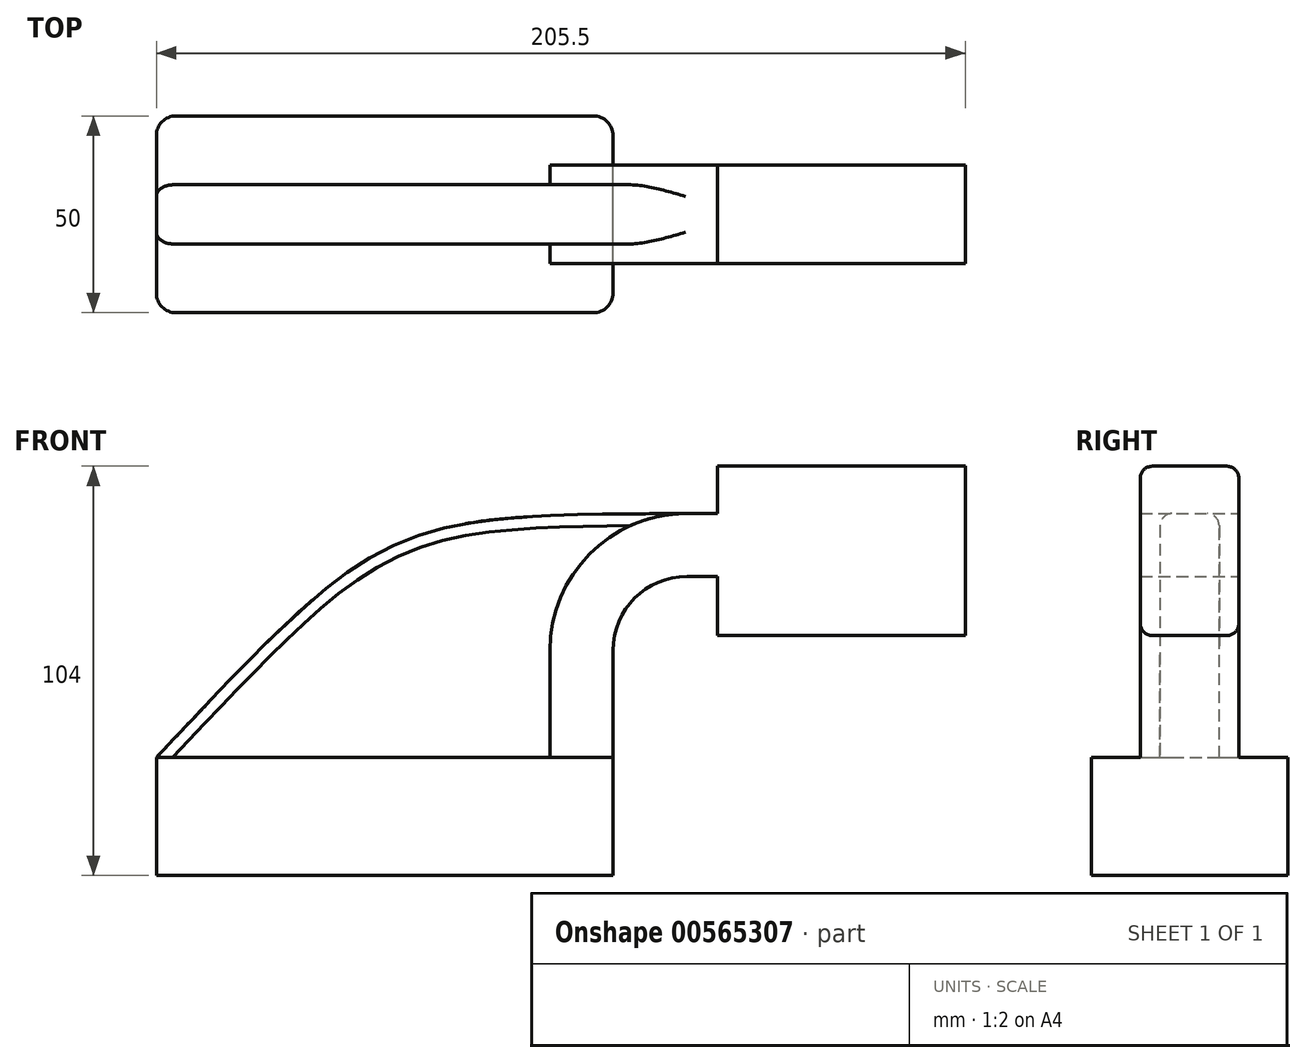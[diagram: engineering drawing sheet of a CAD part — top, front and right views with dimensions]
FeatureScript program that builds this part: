
annotation { "Feature Type Name" : "Feature", "Feature Type Description" : "" }
export const myFeature = defineFeature(function(context is Context, id is Id, definition is map)
    precondition{}
    {
        {
            var Q0;
            Q0=qCreatedBy(makeId("Front.planeOp"),FACE);
            var sketch = newSketch(context, id + "F0", { "sketchPlane" : qUnion([Q0])});
            skLineSegment(sketch, "E0.bottom", {"start": v(58, -15) * mm, "end": v(-58, -15) * mm});
            skLineSegment(sketch, "E0.top", {"start": v(58, 15) * mm, "end": v(-58, 15) * mm});
            skLineSegment(sketch, "E0.left", {"start": v(58, -15) * mm, "end": v(58, 15) * mm});
            skLineSegment(sketch, "E0.right", {"start": v(-58, -15) * mm, "end": v(-58, 15) * mm});
            skPoint(sketch, "E0.middle", {"position": v(0, 0) * mm});
            skLineSegment(sketch, "E1.bottom", {"start": v(147.5, 46) * mm, "end": v(84.5, 46) * mm});
            skLineSegment(sketch, "E1.top", {"start": v(147.5, 89) * mm, "end": v(84.5, 89) * mm});
            skLineSegment(sketch, "E1.left", {"start": v(147.5, 46) * mm, "end": v(147.5, 89) * mm});
            skLineSegment(sketch, "E1.right", {"start": v(84.5, 46) * mm, "end": v(84.5, 89) * mm});
            skPoint(sketch, "E1.middle", {"position": v(116, 67.5) * mm});
            skLineSegment(sketch, "E2", {"start": v(58, 15) * mm, "end": v(58, 42.2) * mm});
            skArc(sketch, "E3", {"start": v(58, 42.2) * mm, "mid": v(63.5, 55.5) * mm, "end": v(76.8, 61) * mm});
            skLineSegment(sketch, "E4", {"start": v(76.8, 61) * mm, "end": v(116.18, 61) * mm});
            skLineSegment(sketch, "E5.0", {"start": v(76.8, 77) * mm, "end": v(116.18, 77) * mm});
            skArc(sketch, "E5.1", {"start": v(42, 42.2) * mm, "mid": v(52.2, 66.8) * mm, "end": v(76.8, 77) * mm});
            skLineSegment(sketch, "E5.2", {"start": v(42, 15) * mm, "end": v(42, 42.2) * mm});
            skLineSegment(sketch, "E6", {"start": v(116.18, 77) * mm, "end": v(116.18, 61) * mm});
            skFitSpline(sketch, "E7", {"points": [v(-58, 15) * mm, v(76.8, 77) * mm], "startDerivative": vector(174, 184.66) * mm, "endDerivative": vector(230.42, 1.34) * mm});
            skSolve(sketch);
        }
        {
            var Q0;
            Q0=makeQuery(id+"F0.imprint","IMPRINT",FACE,{"disambiguationData":[TD([[makeQuery(id+"F0.imprint","IMPRINT",EDGE,{"derivedFrom":sQuery(id+"F0.wireOp",EDGE,"E0.bottom")}),-1.0]])]});
            extrude(context, id + "F1", {"entities" : qUnion([Q0]), "endBound" : BoundingType.SYMMETRIC, "depth" : 50 * mm, "offsetDistance" : 25 * mm});
        }
        {
            var Q0;
            {var subQ1=sQuery(id+"F0.wireOp",EDGE,"E2");Q0=makeQuery(id+"F0.imprint","IMPRINT",FACE,{"disambiguationData":[TD([[makeQuery(id+"F0.imprint","IMPRINT",EDGE,{"derivedFrom":subQ1}),1.0]])]});}
            var Q1;
            {var subQ5=sQuery(id+"F0.wireOp",EDGE,"E6");Q1=makeQuery(id+"F0.imprint","IMPRINT",FACE,{"disambiguationData":[TD([[makeQuery(id+"F0.imprint","IMPRINT",EDGE,{"derivedFrom":subQ5}),-1.0]])]});}
            var Q2;
            {var subQ1=sQuery(id+"F0.wireOp",EDGE,"E1.bottom");Q2=makeQuery(id+"F0.imprint","IMPRINT",FACE,{"disambiguationData":[TD([[makeQuery(id+"F0.imprint","IMPRINT",EDGE,{"derivedFrom":subQ1}),-1.0]])]});}
            extrude(context, id + "F2", {"entities" : qUnion([Q0, Q1, Q2]), "operationType" : NewBodyOperationType.ADD, "endBound" : BoundingType.SYMMETRIC, "depth" : 25 * mm, "offsetDistance" : 25 * mm});
        }
        {
            var Q0;
            {var subQ3=sQuery(id+"F0.wireOp",EDGE,"E5.2");Q0=makeQuery(id+"F0.imprint","IMPRINT",FACE,{"disambiguationData":[TD([[makeQuery(id+"F0.imprint","IMPRINT",EDGE,{"derivedFrom":subQ3}),1.0]])]});}
            extrude(context, id + "F3", {"entities" : qUnion([Q0]), "operationType" : NewBodyOperationType.ADD, "endBound" : BoundingType.SYMMETRIC, "depth" : 15 * mm, "offsetDistance" : 25 * mm});
        }
        {
            var Q0;
            Q0=makeQuery(id+"F1.opExtrude","CAP_EDGE",EDGE,{"disambiguationData":[OSD([sQuery(id+"F0.wireOp",EDGE,"E0.left")])],"isStart":false});
            var Q1;
            Q1=makeQuery(id+"F1.opExtrude","CAP_EDGE",EDGE,{"disambiguationData":[OSD([sQuery(id+"F0.wireOp",EDGE,"E0.right")])],"isStart":false});
            var Q2;
            Q2=makeQuery(id+"F1.opExtrude","CAP_EDGE",EDGE,{"disambiguationData":[OSD([sQuery(id+"F0.wireOp",EDGE,"E0.right")])],"isStart":true});
            var Q3;
            Q3=makeQuery(id+"F1.opExtrude","CAP_EDGE",EDGE,{"disambiguationData":[OSD([sQuery(id+"F0.wireOp",EDGE,"E0.left")])],"isStart":true});
            fillet(context, id + "F4", {"entities" : qUnion([Q0, Q1, Q2, Q3]), "radius" : 5 * mm, "tangentPropagation" : true, "allowEdgeOverflow" : false});
        }
        {
            var Q0;
            Q0=makeQuery(id+"F3.opExtrude","CAP_EDGE",EDGE,{"disambiguationData":[OSD([sQuery(id+"F0.wireOp",EDGE,"E7")])],"isStart":false});
            var Q1;
            Q1=makeQuery(id+"F3.opExtrude","CAP_EDGE",EDGE,{"disambiguationData":[OSD([sQuery(id+"F0.wireOp",EDGE,"E7")])],"isStart":true});
            var Q2;
            Q2=makeQuery(id+"F2.opExtrude","CAP_EDGE",EDGE,{"disambiguationData":[OSD([sQuery(id+"F0.wireOp",EDGE,"E1.top")])],"isStart":false});
            var Q3;
            Q3=makeQuery(id+"F2.opExtrude","CAP_EDGE",EDGE,{"disambiguationData":[OSD([sQuery(id+"F0.wireOp",EDGE,"E1.top")])],"isStart":true});
            var Q4;
            Q4=makeQuery(id+"F2.opExtrude","CAP_EDGE",EDGE,{"disambiguationData":[OSD([sQuery(id+"F0.wireOp",EDGE,"E1.bottom")])],"isStart":false});
            var Q5;
            Q5=makeQuery(id+"F2.opExtrude","CAP_EDGE",EDGE,{"disambiguationData":[OSD([sQuery(id+"F0.wireOp",EDGE,"E1.bottom")])],"isStart":true});
            fillet(context, id + "F5", {"entities" : qUnion([Q0, Q1, Q2, Q3, Q4, Q5]), "radius" : 3 * mm, "tangentPropagation" : true, "allowEdgeOverflow" : false});
        }
    });
